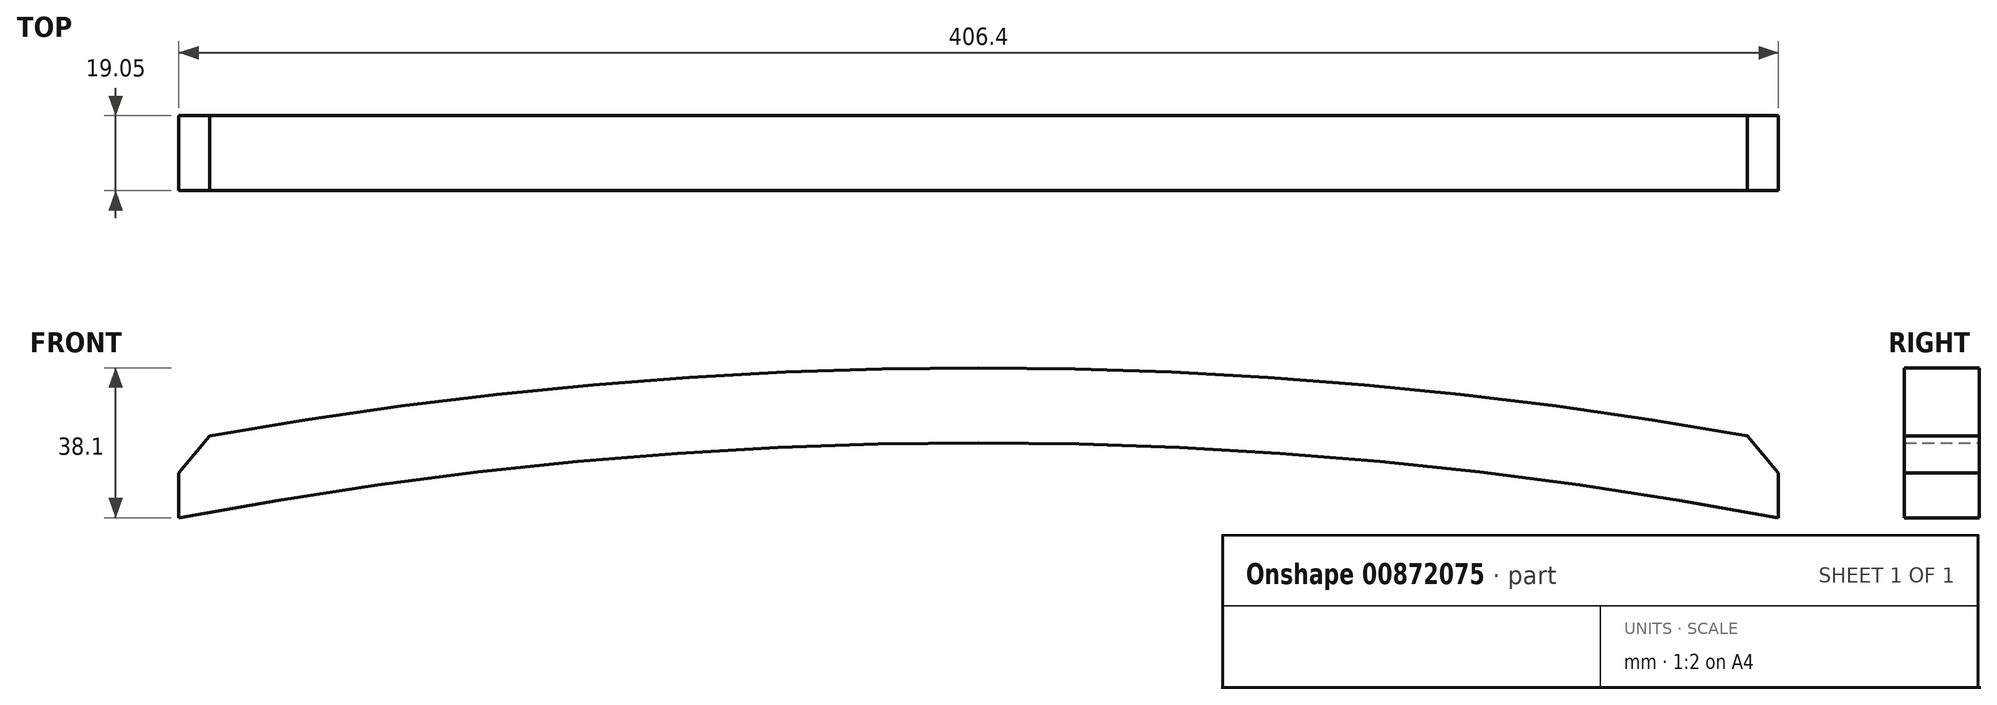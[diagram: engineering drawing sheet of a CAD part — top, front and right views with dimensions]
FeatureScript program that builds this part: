
annotation { "Feature Type Name" : "Feature", "Feature Type Description" : "" }
export const myFeature = defineFeature(function(context is Context, id is Id, definition is map)
    precondition{}
    {
        {
            var Q0;
            Q0=qCreatedBy(makeId("Front.planeOp"),FACE);
            var sketch = newSketch(context, id + "F0", { "sketchPlane" : qUnion([Q0])});
            skLineSegment(sketch, "E0", {"start": v(-203.2, -19.05) * mm, "end": v(203.2, -19.05) * mm, "construction": true});
            skLineSegment(sketch, "E1", {"start": v(0, 0) * mm, "end": v(0, -19.05) * mm, "construction": true});
            skPoint(sketch, "E1.startSnap0", {"position": v(0, -19.05) * mm});
            skArc(sketch, "E2", {"start": v(203.2, -19.05) * mm, "mid": v(0, 0) * mm, "end": v(-203.2, -19.05) * mm});
            skLineSegment(sketch, "E3", {"start": v(-203.2, 19.05) * mm, "end": v(203.2, 19.05) * mm, "construction": true});
            skArc(sketch, "E4.trimOffspring", {"start": v(203.2, 0.33) * mm, "mid": v(0, 19.05) * mm, "end": v(-203.2, 0.33) * mm});
            skLineSegment(sketch, "E5", {"start": v(-203.2, -19.05) * mm, "end": v(-203.2, 0.33) * mm});
            skLineSegment(sketch, "E6", {"start": v(-203.2, 19.05) * mm, "end": v(-203.2, 0.33) * mm, "construction": true});
            skLineSegment(sketch, "E7", {"start": v(203.2, 19.05) * mm, "end": v(203.2, 0.33) * mm, "construction": true});
            skLineSegment(sketch, "E8", {"start": v(203.2, 0.33) * mm, "end": v(203.2, -19.05) * mm});
            skSolve(sketch);
        }
        {
            var Q0;
            Q0=qSketchRegion(id+"F0",true);
            extrude(context, id + "F1", {"entities" : qUnion([Q0]), "depth" : 19.05 * mm});
        }
        {
            var Q0;
            Q0=makeQuery(id+"F1.opExtrude","SWEPT_EDGE",EDGE,{"disambiguationData":[OSD([sQuery(id+"F0.wireOp",EDGE,"E4.trimOffspring"),sQuery(id+"F0.wireOp",EDGE,"E5")])]});
            var Q1;
            Q1=makeQuery(id+"F1.opExtrude","SWEPT_EDGE",EDGE,{"disambiguationData":[OSD([sQuery(id+"F0.wireOp",EDGE,"E4.trimOffspring"),sQuery(id+"F0.wireOp",EDGE,"E8")])]});
            chamfer(context, id + "F2", {"entities" : qUnion([Q0, Q1]), "width" : 9.52 * mm, "tangentPropagation" : true});
        }
    });
